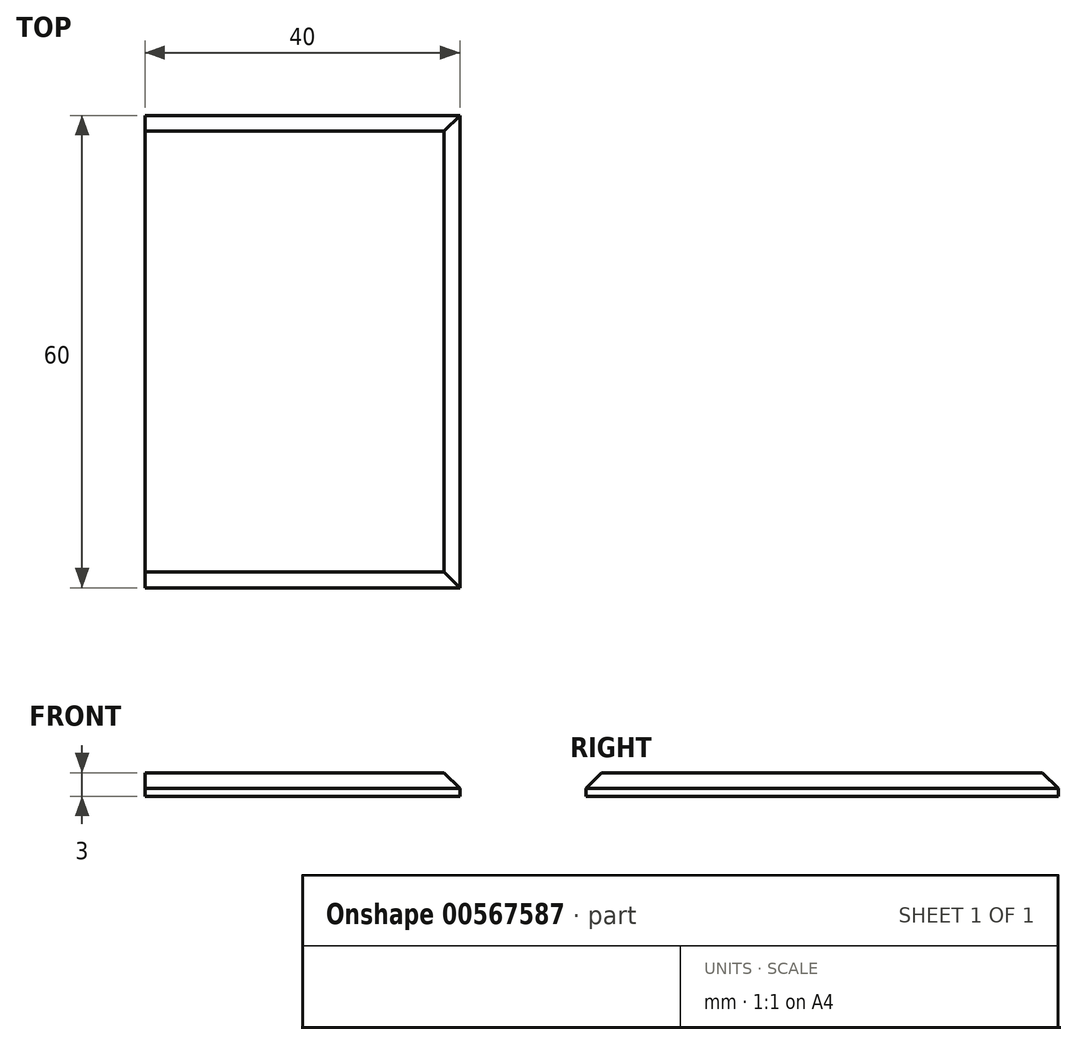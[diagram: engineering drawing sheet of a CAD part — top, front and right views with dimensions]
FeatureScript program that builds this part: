
annotation { "Feature Type Name" : "Feature", "Feature Type Description" : "" }
export const myFeature = defineFeature(function(context is Context, id is Id, definition is map)
    precondition{}
    {
        {
            var Q0;
            Q0=qCreatedBy(makeId("Top.planeOp"),FACE);
            var sketch = newSketch(context, id + "F0", { "sketchPlane" : qUnion([Q0])});
            skLineSegment(sketch, "E0.bottom", {"start": v(20, 30) * mm, "end": v(-20, 30) * mm});
            skLineSegment(sketch, "E0.top", {"start": v(20, -30) * mm, "end": v(-20, -30) * mm});
            skLineSegment(sketch, "E0.left", {"start": v(20, 30) * mm, "end": v(20, -30) * mm});
            skLineSegment(sketch, "E0.right", {"start": v(-20, 30) * mm, "end": v(-20, -30) * mm});
            skPoint(sketch, "E0.middle", {"position": v(0, 0) * mm});
            skSolve(sketch);
        }
        {
            var Q0;
            Q0=makeQuery(id+"F0.imprint","IMPRINT",FACE,{"disambiguationData":[TD([[makeQuery(id+"F0.imprint","IMPRINT",EDGE,{"derivedFrom":sQuery(id+"F0.wireOp",EDGE,"E0.bottom")}),1.0]])]});
            extrude(context, id + "F1", {"entities" : qUnion([Q0]), "depth" : 3 * mm, "offsetDistance" : 25 * mm});
        }
        {
            var Q0;
            Q0=makeQuery(id+"F1.opExtrude","CAP_EDGE",EDGE,{"disambiguationData":[OSD([sQuery(id+"F0.wireOp",EDGE,"E0.top")])],"isStart":false});
            var Q1;
            Q1=makeQuery(id+"F1.opExtrude","CAP_EDGE",EDGE,{"disambiguationData":[OSD([sQuery(id+"F0.wireOp",EDGE,"E0.bottom")])],"isStart":false});
            var Q2;
            Q2=makeQuery(id+"F1.opExtrude","CAP_EDGE",EDGE,{"disambiguationData":[OSD([sQuery(id+"F0.wireOp",EDGE,"E0.left")])],"isStart":false});
            chamfer(context, id + "F2", {"entities" : qUnion([Q0, Q1, Q2]), "width" : 2 * mm, "tangentPropagation" : true});
        }
    });
